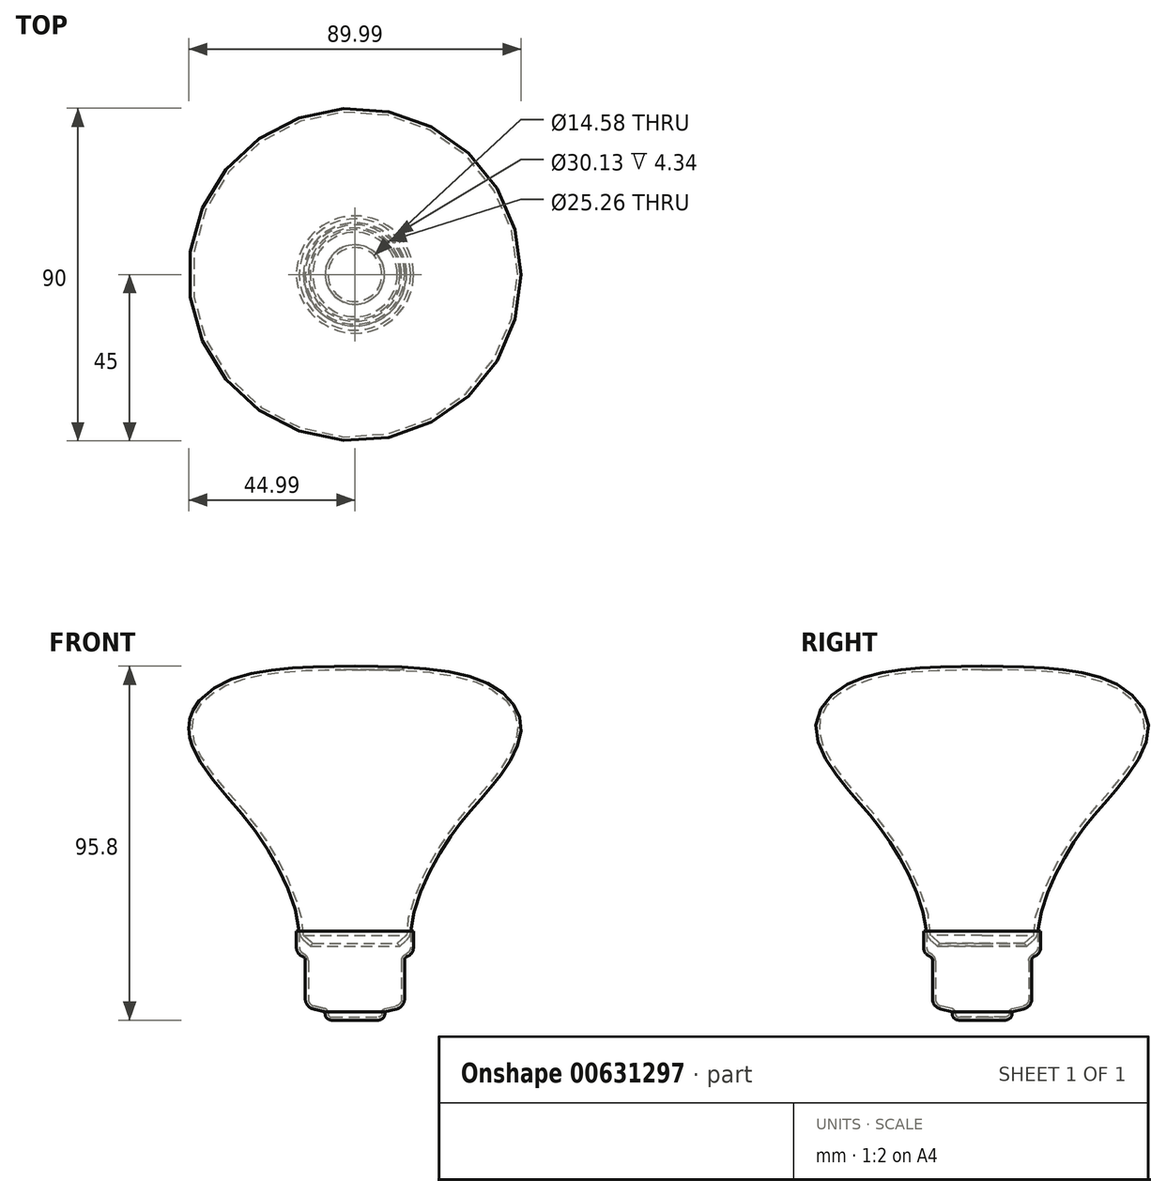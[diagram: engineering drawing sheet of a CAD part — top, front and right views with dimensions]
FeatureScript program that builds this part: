
annotation { "Feature Type Name" : "Feature", "Feature Type Description" : "" }
export const myFeature = defineFeature(function(context is Context, id is Id, definition is map)
    precondition{}
    {
        {
            var Q0;
            Q0=qCreatedBy(makeId("Front.planeOp"),FACE);
            var sketch = newSketch(context, id + "F0", { "sketchPlane" : qUnion([Q0])});
            skLineSegment(sketch, "E0", {"start": v(0, 0) * mm, "end": v(0, 95) * mm, "construction": true});
            skLineSegment(sketch, "E1", {"start": v(0, 95) * mm, "end": v(45, 95) * mm, "construction": true});
            skFitSpline(sketch, "E2", {"points": [v(0, 95) * mm, v(35.35, 90.6) * mm, v(45, 78.32) * mm, v(37.07, 62.53) * mm, v(25.88, 48.88) * mm, v(15, 21.74) * mm], "startDerivative": vector(142.37, 0) * mm, "endDerivative": vector(0, -111.14) * mm});
            skLineSegment(sketch, "E3", {"start": v(15, 21.74) * mm, "end": v(15, 56.48) * mm, "construction": true});
            skLineSegment(sketch, "E4", {"start": v(13.68, 20.61) * mm, "end": v(12.12, 19.28) * mm});
            skArc(sketch, "E5.filletArc", {"start": v(13.68, 20.61) * mm, "mid": v(14.64, 21.84) * mm, "end": v(15.06, 23.34) * mm});
            skLineSegment(sketch, "E6.0", {"start": v(14, 22.2) * mm, "end": v(11.42, 20) * mm});
            skFitSpline(sketch, "E6.1", {"points": [v(0, 94) * mm, v(2.96, 94) * mm, v(9.18, 93.97) * mm, v(18.65, 93.51) * mm, v(26.07, 92.5) * mm, v(31.34, 91.14) * mm, v(34.86, 89.83) * mm, v(37.88, 88.17) * mm, v(40.34, 86.23) * mm, v(42.22, 84.07) * mm, v(43.47, 81.74) * mm, v(43.96, 79.7) * mm, v(44.02, 78.01) * mm, v(43.85, 76.27) * mm, v(43.24, 74) * mm, v(41.97, 71.22) * mm, v(40.3, 68.45) * mm, v(38.4, 65.77) * mm, v(36.38, 63.24) * mm, v(34.41, 60.93) * mm, v(32.47, 58.73) * mm, v(30.53, 56.52) * mm, v(28.56, 54.18) * mm, v(26.88, 52.01) * mm, v(25.5, 50.1) * mm, v(24.44, 48.55) * mm, v(23.37, 46.9) * mm, v(21.94, 44.58) * mm, v(20.18, 41.48) * mm, v(18.22, 37.55) * mm, v(16.5, 33.51) * mm, v(14.69, 28.11) * mm, v(14, 24.19) * mm, v(14, 21.74) * mm]});
            skLineSegment(sketch, "E7", {"start": v(0, 95) * mm, "end": v(0, 94) * mm});
            skLineSegment(sketch, "E8", {"start": v(11.42, 20) * mm, "end": v(12.12, 19.28) * mm});
            skLineSegment(sketch, "E9", {"start": v(45, 78.32) * mm, "end": v(45, 95) * mm, "construction": true});
            skSolve(sketch);
        }
        {
            var Q0;
            Q0=makeQuery(id+"F0.imprint","IMPRINT",FACE,{"disambiguationData":[TD([[makeQuery(id+"F0.imprint","IMPRINT",EDGE,{"derivedFrom":sQuery(id+"F0.wireOp",EDGE,"E2")}),-1.0]])]});
            var Q1;
            Q1=sQuery(id+"F0.wireOp",EDGE,"E0");
            revolve(context, id + "F1", {"entities" : qUnion([Q0]), "axis" : qUnion([Q1]), "revolveType" : RevolveType.FULL});
        }
        {
            var Q0;
            Q0=qCreatedBy(makeId("Front.planeOp"),FACE);
            var sketch = newSketch(context, id + "F2", { "sketchPlane" : qUnion([Q0])});
            skLineSegment(sketch, "E10.0", {"start": v(15.06, 23.34) * mm, "end": v(-15.06, 23.34) * mm, "construction": true});
            skLineSegment(sketch, "E11", {"start": v(15.06, 23.34) * mm, "end": v(15.06, 19) * mm});
            skLineSegment(sketch, "E12", {"start": v(14.13, 17.3) * mm, "end": v(13.56, 16.94) * mm});
            skLineSegment(sketch, "E13", {"start": v(12.63, 15.25) * mm, "end": v(12.63, 4.95) * mm});
            skLineSegment(sketch, "E14", {"start": v(11.1, 3) * mm, "end": v(8.06, 2.27) * mm});
            skLineSegment(sketch, "E15", {"start": v(7.3, 1.3) * mm, "end": v(7.3, 1) * mm});
            skLineSegment(sketch, "E16", {"start": v(6.3, 0) * mm, "end": v(0, 0) * mm});
            skPoint(sketch, "E17.visualSharp", {"position": v(12.63, 16.35) * mm});
            skArc(sketch, "E17.filletArc", {"start": v(13.56, 16.94) * mm, "mid": v(12.88, 16.22) * mm, "end": v(12.63, 15.25) * mm});
            skPoint(sketch, "E18.visualSharp", {"position": v(15.06, 17.9) * mm});
            skArc(sketch, "E18.filletArc", {"start": v(14.13, 17.3) * mm, "mid": v(14.82, 18.03) * mm, "end": v(15.06, 19) * mm});
            skPoint(sketch, "E19.visualSharp", {"position": v(12.63, 3.37) * mm});
            skArc(sketch, "E19.filletArc", {"start": v(11.1, 3) * mm, "mid": v(12.2, 3.7) * mm, "end": v(12.63, 4.95) * mm});
            skPoint(sketch, "E20.visualSharp", {"position": v(7.3, 2.1) * mm});
            skArc(sketch, "E20.filletArc", {"start": v(8.06, 2.27) * mm, "mid": v(7.5, 1.92) * mm, "end": v(7.3, 1.3) * mm});
            skPoint(sketch, "E21.visualSharp", {"position": v(7.3, 0) * mm});
            skArc(sketch, "E21.filletArc", {"start": v(6.3, 0) * mm, "mid": v(7, 0.3) * mm, "end": v(7.3, 1) * mm});
            skLineSegment(sketch, "E22.0", {"start": v(6.3, -0.8) * mm, "end": v(0, -0.8) * mm});
            skArc(sketch, "E22.1", {"start": v(6.3, -0.8) * mm, "mid": v(7.71, -0.1) * mm, "end": v(8.03, 1.45) * mm});
            skLineSegment(sketch, "E22.2", {"start": v(11.28, 2.22) * mm, "end": v(8.03, 1.45) * mm});
            skLineSegment(sketch, "E22.3", {"start": v(15.86, 23.34) * mm, "end": v(15.86, 19) * mm});
            skArc(sketch, "E22.4", {"start": v(14.07, 16.38) * mm, "mid": v(15.37, 17.41) * mm, "end": v(15.86, 19) * mm});
            skLineSegment(sketch, "E22.5", {"start": v(13.43, 15.45) * mm, "end": v(13.43, 4.95) * mm});
            skArc(sketch, "E22.6", {"start": v(11.28, 2.22) * mm, "mid": v(12.83, 3.21) * mm, "end": v(13.43, 4.95) * mm});
            skLineSegment(sketch, "E23", {"start": v(15.86, 23.34) * mm, "end": v(15.06, 23.34) * mm});
            skLineSegment(sketch, "E24", {"start": v(0, -0.8) * mm, "end": v(0, 0) * mm});
            skLineSegment(sketch, "E25", {"start": v(0, 0) * mm, "end": v(0, 23.34) * mm, "construction": true});
            skPoint(sketch, "E26.visualSharp", {"position": v(13.43, 16.22) * mm});
            skArc(sketch, "E26.filletArc", {"start": v(14.07, 16.38) * mm, "mid": v(13.6, 16.02) * mm, "end": v(13.43, 15.45) * mm});
            skSolve(sketch);
        }
        {
            var Q0;
            Q0=makeQuery(id+"F2.imprint","IMPRINT",FACE,{"disambiguationData":[TD([[makeQuery(id+"F2.imprint","IMPRINT",EDGE,{"derivedFrom":sQuery(id+"F2.wireOp",EDGE,"E11")}),1.0]])]});
            var Q1;
            Q1=sQuery(id+"F2.wireOp",EDGE,"E25");
            revolve(context, id + "F3", {"entities" : qUnion([Q0]), "axis" : qUnion([Q1]), "revolveType" : RevolveType.FULL});
        }
    });
